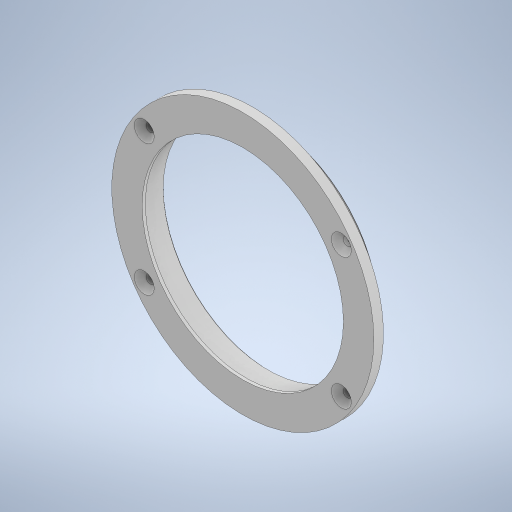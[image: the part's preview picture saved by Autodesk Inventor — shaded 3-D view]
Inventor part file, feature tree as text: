
AUTODESK INVENTOR PART (.ipt)
format: ipt  version: 2023.4 (Build 274418000, 418)  size: 368,640 bytes
history: native  units: mm
features: extrude x8, sketch x3, chamfer x2, projected_geometry x2
ambient origin geometry x8: Origin, YZ Plane, XZ Plane, XY Plane, X Axis, Y Axis, Z Axis, Center Point
bodies: Solid1 (feature_tree)
feature tree (15):
  extrude  "Extrusion1"  Depth=4.6mm
  extrude  "Extrusion2"  Depth=4.6mm
  extrude  "Extrusion3"  Depth=2.0mm TaperAngle=45.0deg
  chamfer  "Chamfer1"  Distance=2.0mm
  extrude  "Extrusion4"  Depth=10.0mm
  extrude  "Extrusion7"  Depth=1.5mm TaperAngle=0.0deg
  extrude  "Extrusion10"  Depth=10.0mm
  chamfer  "Chamfer5"  Distance=4.0mm
  extrude  "Extrusion11"  Depth=10.0mm
  extrude  "Extrusion13"  Depth=10.0mm
  sketch  "Sketch1"  dims[d0=4.6mm d1=0.0mm d2=100.1mm]
  projected_geometry  "Projected Loop1"
  sketch  "Sketch12"  dims[d3=4.6mm d4=0.0mm d5=105.0mm]
  sketch  "Sketch14"  dims[d6=8.0mm d7=0.0mm d8=0.5mm d9=2.0mm d10=45.0deg d11=2.0mm d12=0.0mm d29=96.0mm d30=1.5mm d31=0.0mm d55=4.0mm d56=4.0mm d57=4.0mm d58=4.0mm d59=10.0mm d60=0.0mm d61=2.8mm d62=2.0mm d63=45.0deg d64=0.0mm d65=0.0mm d72=123.0mm d73=1.0mm d74=10.0mm d75=0.0mm]
  projected_geometry  "Projected Loop3"
